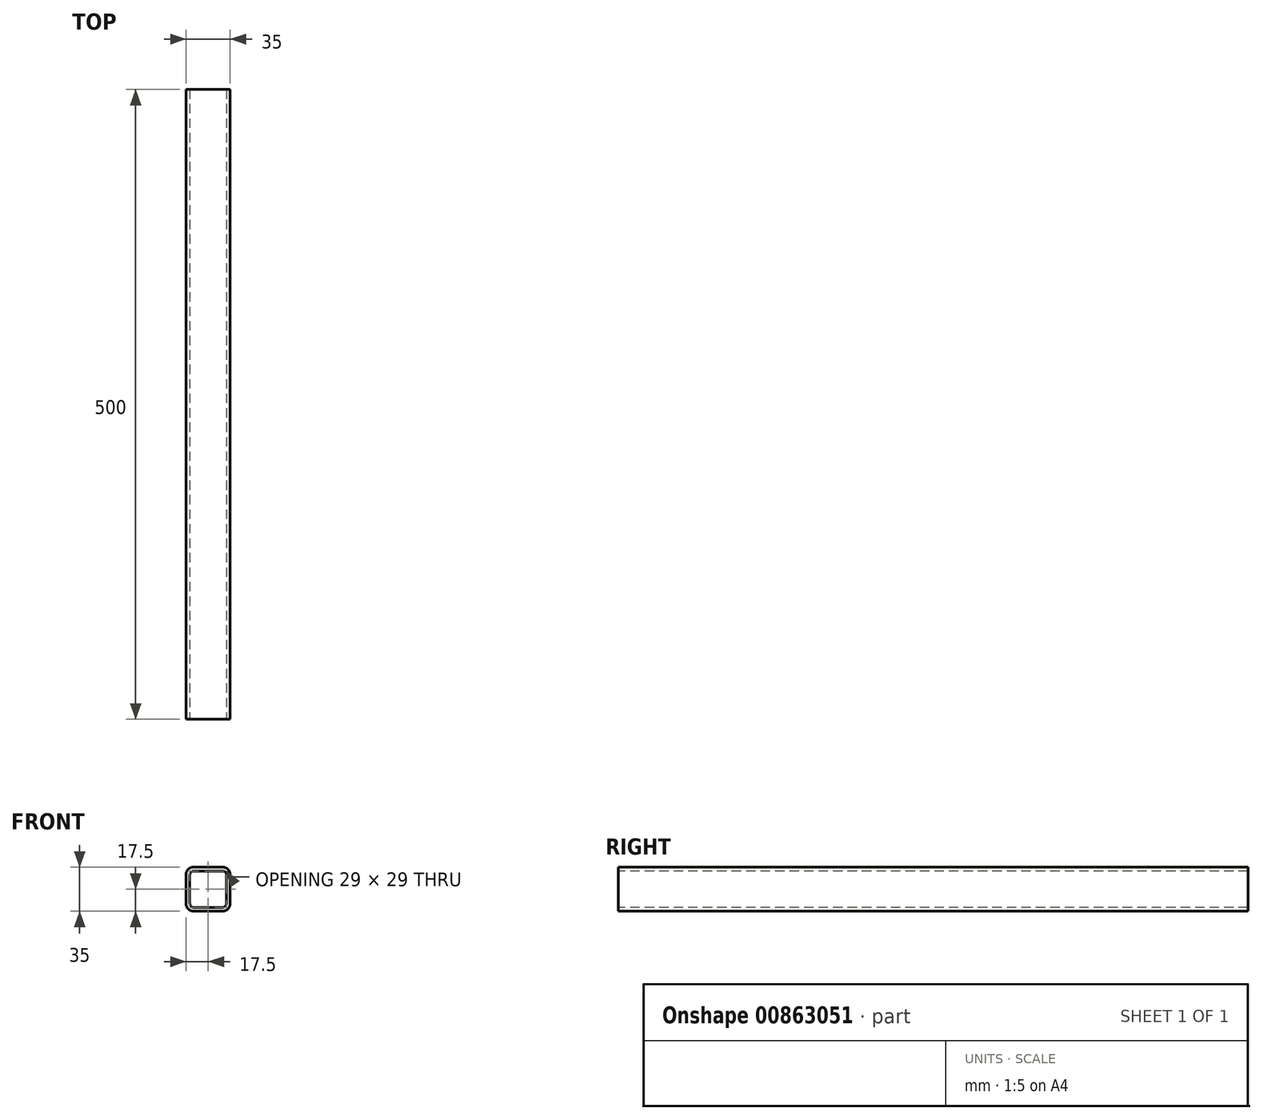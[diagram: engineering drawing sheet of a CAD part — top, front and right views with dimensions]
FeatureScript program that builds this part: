
annotation { "Feature Type Name" : "Feature", "Feature Type Description" : "" }
export const myFeature = defineFeature(function(context is Context, id is Id, definition is map)
    precondition{}
    {
        {
            var Q0;
            Q0=qCreatedBy(makeId("Front.planeOp"),FACE);
            var sketch = newSketch(context, id + "F0", { "sketchPlane" : qUnion([Q0])});
            skLineSegment(sketch, "E0.bottom", {"start": v(11.5, -17.5) * mm, "end": v(-11.5, -17.5) * mm});
            skLineSegment(sketch, "E0.top", {"start": v(11.5, 17.5) * mm, "end": v(-11.5, 17.5) * mm});
            skLineSegment(sketch, "E0.left", {"start": v(17.5, -11.5) * mm, "end": v(17.5, 11.5) * mm});
            skLineSegment(sketch, "E0.right", {"start": v(-17.5, -11.5) * mm, "end": v(-17.5, 11.5) * mm});
            skPoint(sketch, "E0.middle", {"position": v(0, 0) * mm});
            skPoint(sketch, "E1.visualSharp", {"position": v(-17.5, 17.5) * mm});
            skArc(sketch, "E1.filletArc", {"start": v(-11.5, 17.5) * mm, "mid": v(-15.74, 15.74) * mm, "end": v(-17.5, 11.5) * mm});
            skPoint(sketch, "E2.visualSharp", {"position": v(17.5, 17.5) * mm});
            skArc(sketch, "E2.filletArc", {"start": v(17.5, 11.5) * mm, "mid": v(15.74, 15.74) * mm, "end": v(11.5, 17.5) * mm});
            skPoint(sketch, "E3.visualSharp", {"position": v(17.5, -17.5) * mm});
            skArc(sketch, "E3.filletArc", {"start": v(11.5, -17.5) * mm, "mid": v(15.74, -15.74) * mm, "end": v(17.5, -11.5) * mm});
            skPoint(sketch, "E4.visualSharp", {"position": v(-17.5, -17.5) * mm});
            skArc(sketch, "E4.filletArc", {"start": v(-17.5, -11.5) * mm, "mid": v(-15.74, -15.74) * mm, "end": v(-11.5, -17.5) * mm});
            skArc(sketch, "E5.0", {"start": v(11.5, -14.5) * mm, "mid": v(13.62, -13.62) * mm, "end": v(14.5, -11.5) * mm});
            skLineSegment(sketch, "E5.1", {"start": v(11.5, -14.5) * mm, "end": v(-11.5, -14.5) * mm});
            skLineSegment(sketch, "E5.2", {"start": v(14.5, -11.5) * mm, "end": v(14.5, 11.5) * mm});
            skArc(sketch, "E5.3", {"start": v(-14.5, -11.5) * mm, "mid": v(-13.62, -13.62) * mm, "end": v(-11.5, -14.5) * mm});
            skArc(sketch, "E5.4", {"start": v(14.5, 11.5) * mm, "mid": v(13.62, 13.62) * mm, "end": v(11.5, 14.5) * mm});
            skLineSegment(sketch, "E5.5", {"start": v(11.5, 14.5) * mm, "end": v(-11.5, 14.5) * mm});
            skArc(sketch, "E5.6", {"start": v(-11.5, 14.5) * mm, "mid": v(-13.62, 13.62) * mm, "end": v(-14.5, 11.5) * mm});
            skLineSegment(sketch, "E5.7", {"start": v(-14.5, -11.5) * mm, "end": v(-14.5, 11.5) * mm});
            skSolve(sketch);
        }
        {
            assignVariable(context, id + "F1", {"name" : "Length", "anyValue" : 500});
        }
        {
            var Q0;
            Q0=makeQuery(id+"F0.imprint","IMPRINT",FACE,{"disambiguationData":[TD([[makeQuery(id+"F0.imprint","IMPRINT",EDGE,{"derivedFrom":sQuery(id+"F0.wireOp",EDGE,"E0.bottom")}),-1.0]])]});
            extrude(context, id + "F2", {"entities" : qUnion([Q0]), "oppositeDirection" : true, "depth" : (getVariable(context, 'Length')) * mm, "offsetDistance" : 25 * mm});
        }
    });
